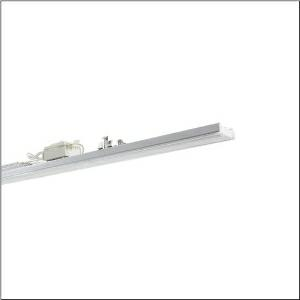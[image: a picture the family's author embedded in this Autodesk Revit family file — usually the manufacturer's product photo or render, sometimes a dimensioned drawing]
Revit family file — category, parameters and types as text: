
# Revit family: licross_r__11_recessed_mo_51tl18vn465g_30d7
name_source: partatom
category: Lighting Fixtures
units: mm (PartAtom-declared; Revit-internal decimal feet)

## family parameters
Cut with Voids When Loaded = No
Host = Face
Light Source = No
Part Type = Normal
Room Calculation Point = No
Round Connector Dimension = Use Diameter
Shared = No

## types (1)
- --- (1 x LED, 6520 lm, 36 W, 4000K)
    Apparent Load = 36 VA
    CIE Flux Codes = 83 96 99 100 100
    Color Rendering = 80
    Color Temperature = 4000K
    Default Elevation = 1800 mm
    Description = Licross® 11 Recessed MO, luminaire insert, of sheet steel, galvanised, coil coated, white, length: 1.500mm, width: 66mm, height: 67mm, LED rated luminous flux: 6.520lm, light colour: 840, control gear: DALI 2, CLO, with plug, 5-pole, with phase selection, mains connection: 220..240V, AC, 50/60Hz, start of lifetime: 36W, end of service life: 41W, internal wiring halogen-free, primary optical cover: cover, of PMMA, light emission: direct distribution, primary light characteristic: symmetric, protection rating (complete): IP40, insulation class (complete): insulation class I (protective earthing), certification: CE, ENEC, VDE, UKCA, protection symbol: D if used in an environment without relevant dust loads with corresponding accessories, impact resistance: IK06, permissible ambient temperature for indoor applications: -25..+40°C, corresponds to IFS (International Featured Standards) requirements for safety and quality in the food industry, reducing of maximum allowable ambient temperature of 5°C with ceiling mounting, LABS conformity tested according to VDMA 24364:2018-05, packaging unit: 1 piece
    Height = 58 mm
    Lamp = 1 x LED
    Lamp Light Flux = 6520 lm
    Lamp Power = 36 W
    Lamp count = 1
    Length = 1500 mm
    Luminous efficacy = 181 lm/W
    Manufacturer = Siteco
    ModVariant = No
    Model = 51TL18VN465G
    Mounting Place = Ceiling
    Mounting Type = Pendant
    Number of Poles = 1
    OnlyDefault = Yes
    Power Factor = 1
    Product Name = Licross® 11 Recessed MO
    Product group = luminaire insert | ceiling pendant
    ProductGroupID = 902
    Protection Class = Protection class I
    Protection Degree = IP 40
    RLX_Detail_Level = 1
    RLX_Emergency_Light_Flux = 0 lm
    RLX_Emergency_Type = 0
    RLX_Emergency_Type_DB = No
    RlxData = <blob elided: 24501 chars, md5=f9983e98>
    Socket = socket
    Standby Power = 0 W
    System Light Flux = 6520 lm
    System Power = 36 W
    Type Comments = factory setting: luminous flux: 100 % | dim-lin: 254 | 240 mA
    Type Image = l_1296930.jpg
    URL = http://relux.com
    VarID = @adj_108649
    Voltage = 0 V
    Weight = 0.00 kg
    Width = 66 mm

## geometry (parser evidence)
native form markers: Blend x4, Sweep x11
no freeform markers — native parametric forms only
